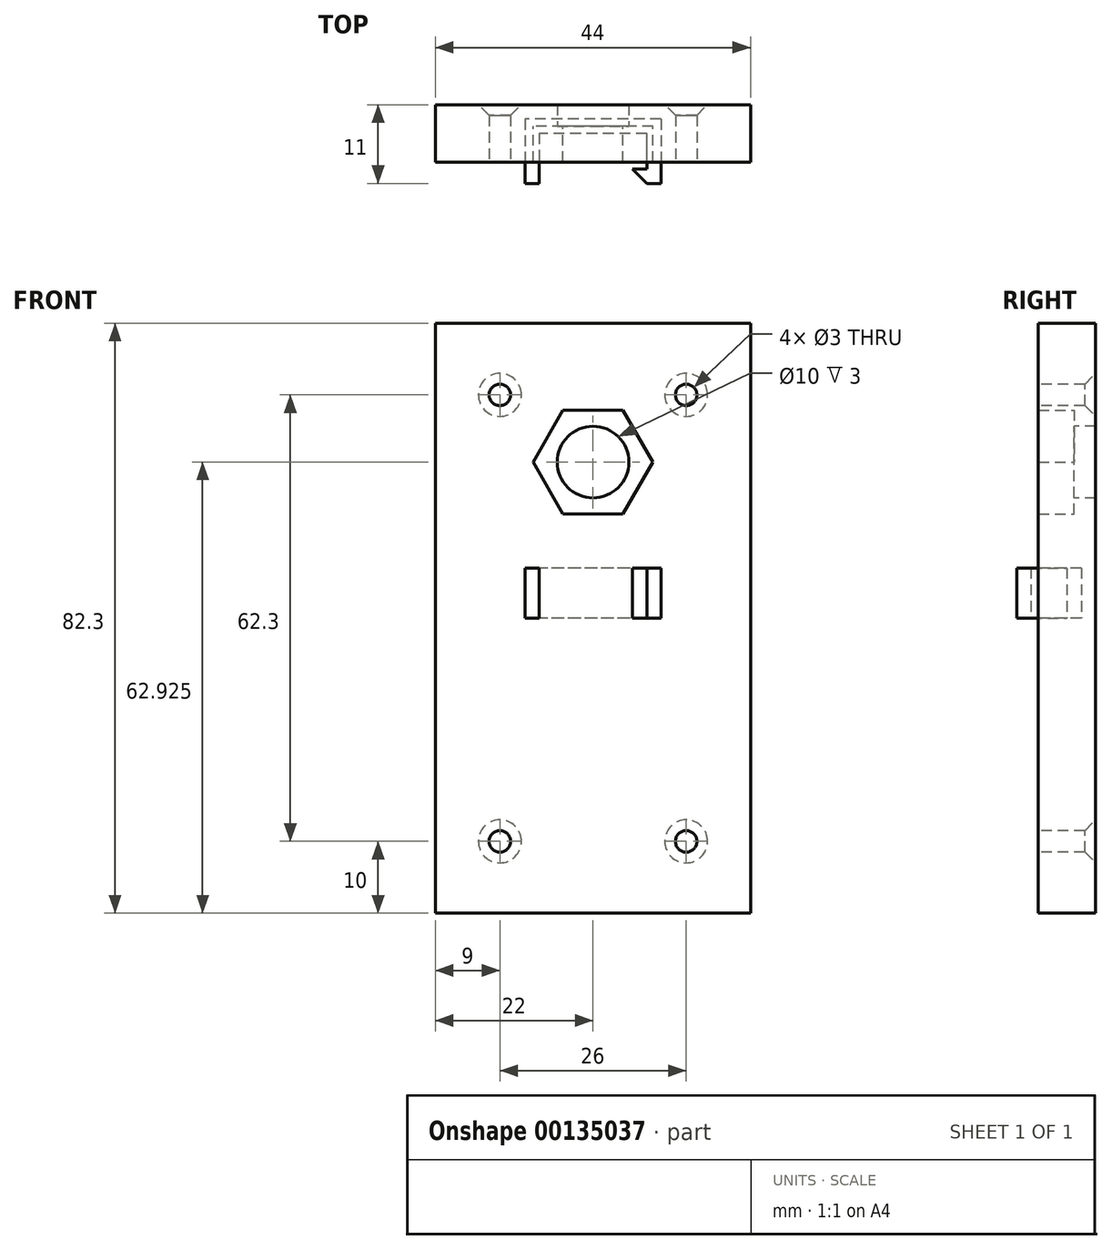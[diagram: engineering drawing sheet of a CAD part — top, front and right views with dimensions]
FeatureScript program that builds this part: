
annotation { "Feature Type Name" : "Feature", "Feature Type Description" : "" }
export const myFeature = defineFeature(function(context is Context, id is Id, definition is map)
    precondition{}
    {
        {
            var Q0;
            Q0=qCreatedBy(makeId("Front.planeOp"),FACE);
            var sketch = newSketch(context, id + "F0", { "sketchPlane" : qUnion([Q0])});
            skLineSegment(sketch, "E0.bottom", {"start": v(13, 31.15) * mm, "end": v(-13, 31.15) * mm, "construction": true});
            skLineSegment(sketch, "E0.top", {"start": v(13, -31.15) * mm, "end": v(-13, -31.15) * mm, "construction": true});
            skLineSegment(sketch, "E0.left", {"start": v(13, 31.15) * mm, "end": v(13, -31.15) * mm, "construction": true});
            skLineSegment(sketch, "E0.right", {"start": v(-13, 31.15) * mm, "end": v(-13, -31.15) * mm, "construction": true});
            skPoint(sketch, "E0.middle", {"position": v(0, 0) * mm});
            skCircle(sketch, "E1", {"center": v(-13, 31.15) * mm, "radius": 1.5 * mm});
            skCircle(sketch, "E2", {"center": v(13, 31.15) * mm, "radius": 1.5 * mm});
            skCircle(sketch, "E3", {"center": v(-13, -31.15) * mm, "radius": 1.5 * mm});
            skCircle(sketch, "E4", {"center": v(13, -31.15) * mm, "radius": 1.5 * mm});
            skLineSegment(sketch, "E5.bottom", {"start": v(22, 41.15) * mm, "end": v(-22, 41.15) * mm});
            skLineSegment(sketch, "E5.top", {"start": v(22, -41.15) * mm, "end": v(-22, -41.15) * mm});
            skLineSegment(sketch, "E5.left", {"start": v(22, 41.15) * mm, "end": v(22, -41.15) * mm});
            skLineSegment(sketch, "E5.right", {"start": v(-22, 41.15) * mm, "end": v(-22, -41.15) * mm});
            skLineSegment(sketch, "E6", {"start": v(0, -31.15) * mm, "end": v(0, -41.15) * mm, "construction": true});
            skLineSegment(sketch, "E7", {"start": v(-22, 2.4) * mm, "end": v(22, 2.4) * mm, "construction": true});
            skLineSegment(sketch, "E8", {"start": v(0, 2.4) * mm, "end": v(0, 41.15) * mm, "construction": true});
            skCircle(sketch, "E9", {"center": v(0, 21.78) * mm, "radius": 5 * mm});
            skCircle(sketch, "E10.cCircle", {"center": v(0, 21.78) * mm, "radius": 7.25 * mm, "construction": true});
            skLineSegment(sketch, "E10.0", {"start": v(-8.37, 21.78) * mm, "end": v(-4.19, 29.02) * mm});
            skLineSegment(sketch, "E10.1", {"start": v(-4.19, 29.02) * mm, "end": v(4.19, 29.02) * mm});
            skLineSegment(sketch, "E10.2", {"start": v(4.19, 29.02) * mm, "end": v(8.37, 21.77) * mm});
            skLineSegment(sketch, "E10.3", {"start": v(8.37, 21.77) * mm, "end": v(4.19, 14.52) * mm});
            skLineSegment(sketch, "E10.4", {"start": v(4.19, 14.52) * mm, "end": v(-4.19, 14.53) * mm});
            skLineSegment(sketch, "E10.5", {"start": v(-4.19, 14.52) * mm, "end": v(-8.37, 21.77) * mm});
            skPoint(sketch, "E10.0.midPoint", {"position": v(-6.28, 25.4) * mm});
            skSolve(sketch);
        }
        {
            var Q0;
            Q0=makeQuery(id+"F0.imprint","IMPRINT",FACE,{"disambiguationData":[TD([[makeQuery(id+"F0.imprint","IMPRINT",EDGE,{"derivedFrom":sQuery(id+"F0.wireOp",EDGE,"E1")}),-1.0]])]});
            var Q1;
            Q1=makeQuery(id+"F0.imprint","IMPRINT",FACE,{"disambiguationData":[TD([[makeQuery(id+"F0.imprint","IMPRINT",EDGE,{"derivedFrom":sQuery(id+"F0.wireOp",EDGE,"E9")}),-1.0]])]});
            extrude(context, id + "F1", {"entities" : qUnion([Q0, Q1]), "oppositeDirection" : true, "depth" : 3 * mm});
        }
        {
            var Q0;
            Q0=makeQuery(id+"F0.imprint","IMPRINT",FACE,{"disambiguationData":[TD([[makeQuery(id+"F0.imprint","IMPRINT",EDGE,{"derivedFrom":sQuery(id+"F0.wireOp",EDGE,"E1")}),-1.0]])]});
            extrude(context, id + "F2", {"entities" : qUnion([Q0]), "operationType" : NewBodyOperationType.ADD, "depth" : 5 * mm});
        }
        {
            var Q0;
            Q0=makeQuery(id+"F1.opExtrude","CAP_EDGE",EDGE,{"disambiguationData":[OSD([sQuery(id+"F0.wireOp",EDGE,"E2")])],"isStart":false});
            var Q1;
            Q1=makeQuery(id+"F1.opExtrude","CAP_EDGE",EDGE,{"disambiguationData":[OSD([sQuery(id+"F0.wireOp",EDGE,"E1")])],"isStart":false});
            var Q2;
            Q2=makeQuery(id+"F1.opExtrude","CAP_EDGE",EDGE,{"disambiguationData":[OSD([sQuery(id+"F0.wireOp",EDGE,"E3")])],"isStart":false});
            var Q3;
            Q3=makeQuery(id+"F1.opExtrude","CAP_EDGE",EDGE,{"disambiguationData":[OSD([sQuery(id+"F0.wireOp",EDGE,"E4")])],"isStart":false});
            chamfer(context, id + "F3", {"entities" : qUnion([Q0, Q1, Q2, Q3]), "width" : 1.5 * mm, "tangentPropagation" : true});
        }
        {
            var Q0;
            Q0=qCreatedBy(makeId("Top.planeOp"),FACE);
            var sketch = newSketch(context, id + "F4", { "sketchPlane" : qUnion([Q0])});
            skLineSegment(sketch, "E11.bottom", {"start": v(7.5, 1) * mm, "end": v(-7.5, 1) * mm});
            skLineSegment(sketch, "E11.top", {"start": v(7.5, -1) * mm, "end": v(-7.5, -1) * mm});
            skLineSegment(sketch, "E11.left", {"start": v(7.5, 1) * mm, "end": v(7.5, -1) * mm});
            skLineSegment(sketch, "E11.right", {"start": v(-7.5, 1) * mm, "end": v(-7.5, -1) * mm});
            skPoint(sketch, "E11.middle", {"position": v(0, 0) * mm});
            skLineSegment(sketch, "E12.bottom", {"start": v(-7.5, 1) * mm, "end": v(-9.5, 1) * mm});
            skLineSegment(sketch, "E12.top", {"start": v(-7.5, -8) * mm, "end": v(-9.5, -8) * mm});
            skLineSegment(sketch, "E12.left", {"start": v(-7.5, 1) * mm, "end": v(-7.5, -8) * mm});
            skLineSegment(sketch, "E12.right", {"start": v(-9.5, 1) * mm, "end": v(-9.5, -8) * mm});
            skLineSegment(sketch, "E13.bottom", {"start": v(7.5, 1) * mm, "end": v(9.5, 1) * mm});
            skLineSegment(sketch, "E13.top", {"start": v(7.5, -8) * mm, "end": v(9.5, -8) * mm});
            skLineSegment(sketch, "E13.right", {"start": v(9.5, 1) * mm, "end": v(9.5, -8) * mm});
            skLineSegment(sketch, "E14", {"start": v(-7.5, -8) * mm, "end": v(-7.5, -6) * mm});
            skLineSegment(sketch, "E15", {"start": v(-7.5, -6) * mm, "end": v(-5.5, -6) * mm});
            skLineSegment(sketch, "E16", {"start": v(-5.5, -6) * mm, "end": v(-7.5, -8) * mm});
            skLineSegment(sketch, "E17", {"start": v(7.5, -8) * mm, "end": v(7.5, -6) * mm});
            skLineSegment(sketch, "E18", {"start": v(7.5, -6) * mm, "end": v(5.5, -6) * mm});
            skLineSegment(sketch, "E19", {"start": v(5.5, -6) * mm, "end": v(7.5, -8) * mm});
            skLineSegment(sketch, "E20", {"start": v(7.5, -6) * mm, "end": v(7.5, -1) * mm});
            skSolve(sketch);
        }
        {
            var Q0;
            {var subQ3=sQuery(id+"F4.wireOp",EDGE,"E12.bottom");Q0=makeQuery(id+"F4.imprint","IMPRINT",FACE,{"disambiguationData":[TD([[makeQuery(id+"F4.imprint","IMPRINT",EDGE,{"derivedFrom":subQ3}),1.0]])]});}
            var Q1;
            Q1=makeQuery(id+"F4.imprint","IMPRINT",FACE,{"disambiguationData":[TD([[makeQuery(id+"F4.imprint","IMPRINT",EDGE,{"derivedFrom":sQuery(id+"F4.wireOp",EDGE,"E14")}),-1.0]])]});
            var Q2;
            {var subQ0=sQuery(id+"F4.wireOp",EDGE,"E11.bottom");Q2=makeQuery(id+"F4.imprint","IMPRINT",FACE,{"disambiguationData":[TD([[makeQuery(id+"F4.imprint","IMPRINT",EDGE,{"derivedFrom":subQ0}),1.0]])]});}
            var Q3;
            Q3=makeQuery(id+"F4.imprint","IMPRINT",FACE,{"disambiguationData":[TD([[makeQuery(id+"F4.imprint","IMPRINT",EDGE,{"derivedFrom":sQuery(id+"F4.wireOp",EDGE,"E11.left")}),1.0]])]});
            var Q4;
            Q4=makeQuery(id+"F4.imprint","IMPRINT",FACE,{"disambiguationData":[TD([[makeQuery(id+"F4.imprint","IMPRINT",EDGE,{"derivedFrom":sQuery(id+"F4.wireOp",EDGE,"E17")}),1.0]])]});
            extrude(context, id + "F5", {"entities" : qUnion([Q0, Q1, Q2, Q3, Q4]), "depth" : 7 * mm});
        }
    });
